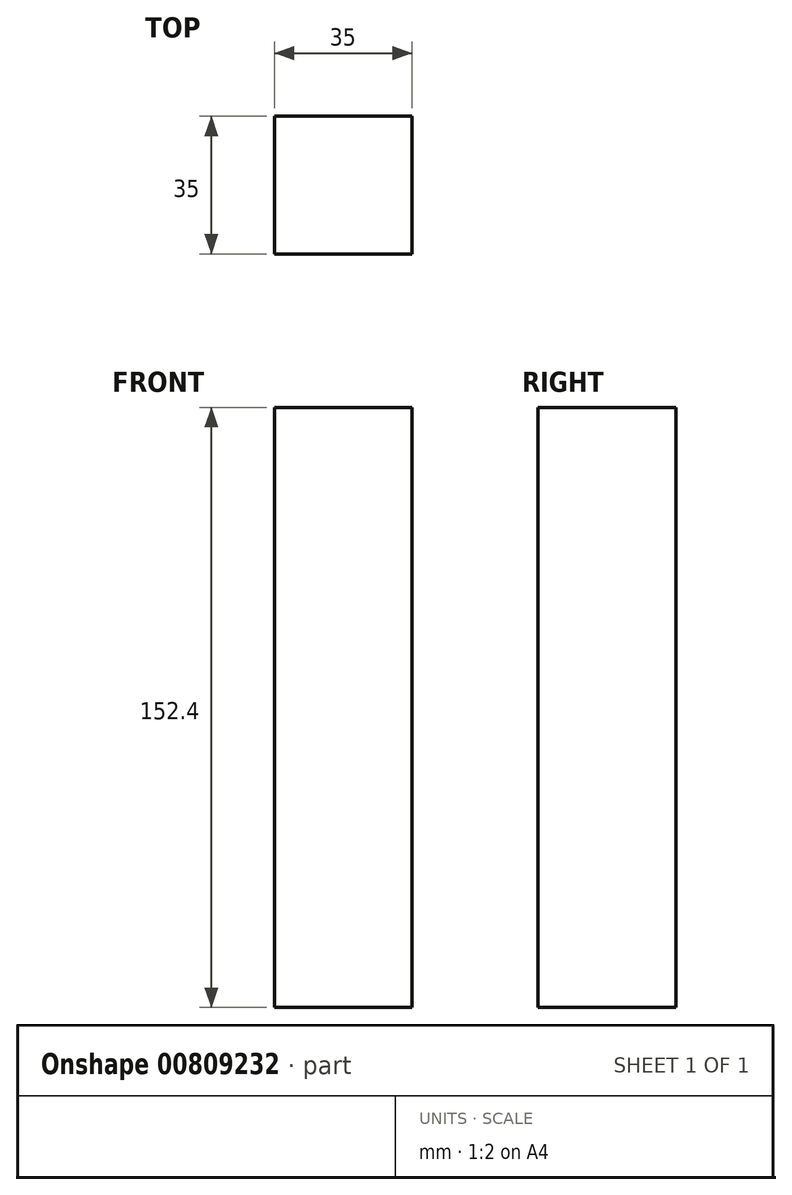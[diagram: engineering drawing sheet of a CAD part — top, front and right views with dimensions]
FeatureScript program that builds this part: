
annotation { "Feature Type Name" : "Feature", "Feature Type Description" : "" }
export const myFeature = defineFeature(function(context is Context, id is Id, definition is map)
    precondition{}
    {
        {
            var Q0;
            Q0=qCreatedBy(makeId("Top.planeOp"),FACE);
            var sketch = newSketch(context, id + "F0", { "sketchPlane" : qUnion([Q0])});
            skLineSegment(sketch, "E0.bottom", {"start": v(17.5, -17.5) * mm, "end": v(-17.5, -17.5) * mm});
            skLineSegment(sketch, "E0.top", {"start": v(17.5, 17.5) * mm, "end": v(-17.5, 17.5) * mm});
            skLineSegment(sketch, "E0.left", {"start": v(17.5, -17.5) * mm, "end": v(17.5, 17.5) * mm});
            skLineSegment(sketch, "E0.right", {"start": v(-17.5, -17.5) * mm, "end": v(-17.5, 17.5) * mm});
            skPoint(sketch, "E0.middle", {"position": v(0, 0) * mm});
            skSolve(sketch);
        }
        {
            var Q0;
            Q0=makeQuery(id+"F0.imprint","IMPRINT",FACE,{"disambiguationData":[TD([[makeQuery(id+"F0.imprint","IMPRINT",EDGE,{"derivedFrom":sQuery(id+"F0.wireOp",EDGE,"E0.bottom")}),-1.0]])]});
            extrude(context, id + "F1", {"entities" : qUnion([Q0]), "depth" : 152.4 * mm, "offsetDistance" : 25.4 * mm});
        }
    });
